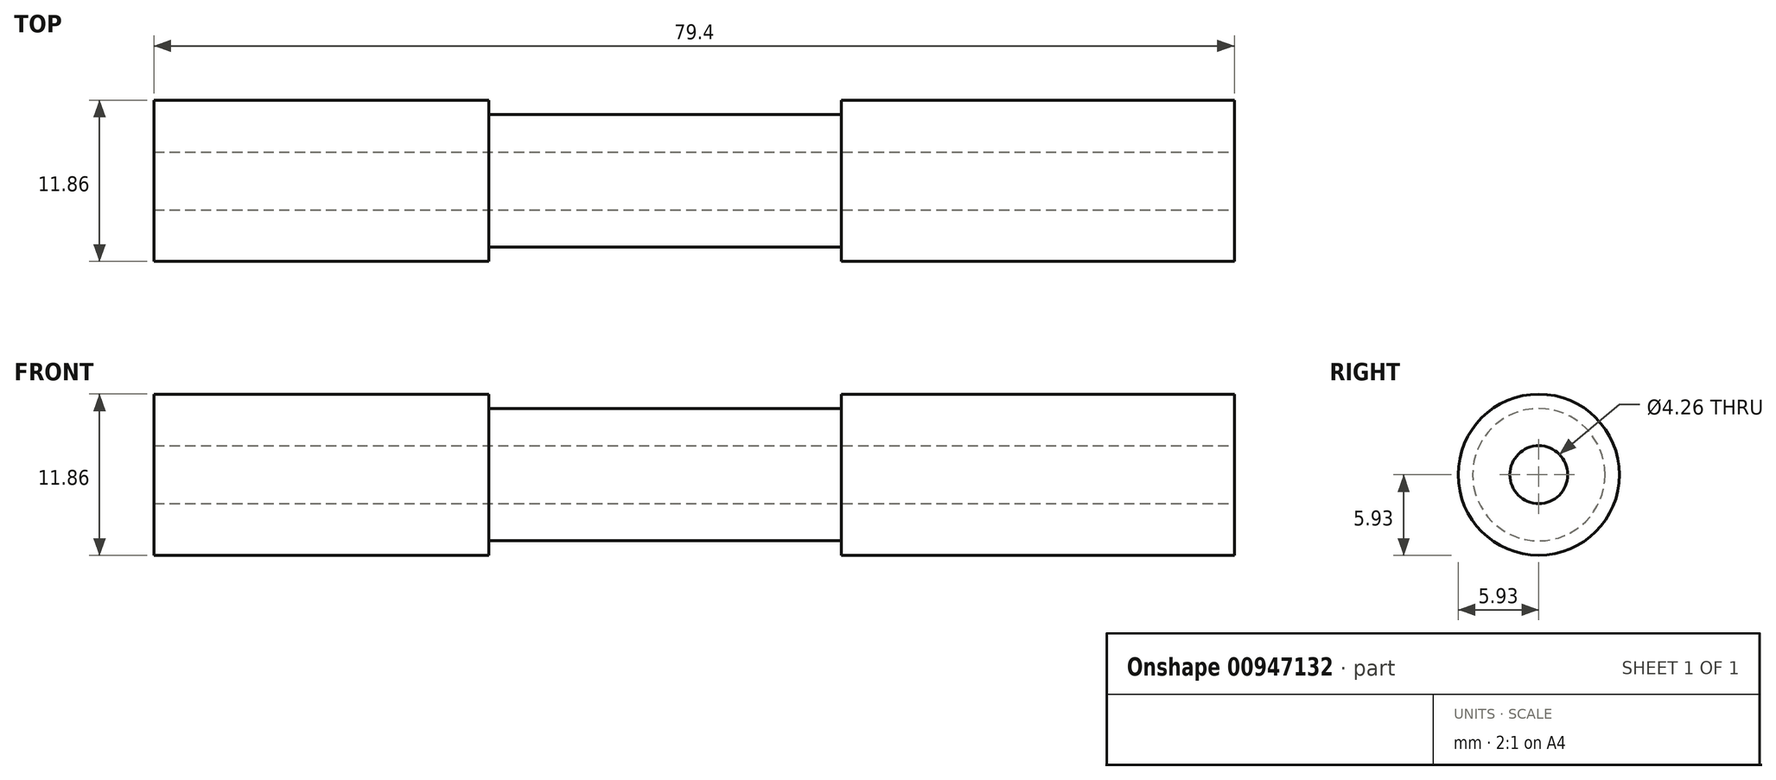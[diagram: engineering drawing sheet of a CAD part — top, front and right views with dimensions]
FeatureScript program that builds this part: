
annotation { "Feature Type Name" : "Feature", "Feature Type Description" : "" }
export const myFeature = defineFeature(function(context is Context, id is Id, definition is map)
    precondition{}
    {
        {
            var Q0;
            Q0=qCreatedBy(makeId("Right.planeOp"),FACE);
            var sketch = newSketch(context, id + "F0", { "sketchPlane" : qUnion([Q0])});
            skCircle(sketch, "E0", {"center": v(0, 0) * mm, "radius": 5.92 * mm});
            skSolve(sketch);
        }
        {
            var Q0;
            Q0=makeQuery(id+"F0.imprint","IMPRINT",FACE,{"disambiguationData":[TD([[makeQuery(id+"F0.imprint","IMPRINT",EDGE,{"derivedFrom":sQuery(id+"F0.wireOp",EDGE,"E0")}),1.0]])]});
            var Q1;
            Q1=sQuery(id+"F0.wireOp",EDGE,"E0");
            extrude(context, id + "F1", {"entities" : qUnion([Q0]), "surfaceEntities" : qUnion([Q1]), "depth" : 24.6 * mm, "offsetDistance" : 25 * mm});
        }
        {
            var Q0;
            Q0=makeQuery(id+"F1.opExtrude","CAP_FACE",FACE,{"disambiguationData":[OSD([sQuery(id+"F0.wireOp",EDGE,"E0")])],"isStart":false});
            var sketch = newSketch(context, id + "F2", { "sketchPlane" : qUnion([Q0])});
            skCircle(sketch, "E1", {"center": v(0, 0) * mm, "radius": 4.87 * mm});
            skSolve(sketch);
        }
        {
            var Q0;
            Q0=makeQuery(id+"F2.imprint","IMPRINT",FACE,{"disambiguationData":[TD([[makeQuery(id+"F2.imprint","IMPRINT",EDGE,{"derivedFrom":sQuery(id+"F2.wireOp",EDGE,"E1")}),1.0]])]});
            var Q1;
            Q1=sQuery(id+"F2.wireOp",EDGE,"E1");
            extrude(context, id + "F3", {"entities" : qUnion([Q0]), "operationType" : NewBodyOperationType.ADD, "surfaceEntities" : qUnion([Q1]), "depth" : 25.9 * mm, "offsetDistance" : 25 * mm});
        }
        {
            var Q0;
            Q0=makeQuery(id+"F3.opExtrude","CAP_FACE",FACE,{"disambiguationData":[OSD([sQuery(id+"F2.wireOp",EDGE,"E1")])],"isStart":false});
            var sketch = newSketch(context, id + "F4", { "sketchPlane" : qUnion([Q0])});
            skCircle(sketch, "E2", {"center": v(0, 0) * mm, "radius": 5.92 * mm});
            skSolve(sketch);
        }
        {
            var Q0;
            Q0=makeQuery(id+"F4.imprint","IMPRINT",FACE,{"disambiguationData":[TD([[makeQuery(id+"F4.imprint","IMPRINT",EDGE,{"derivedFrom":sQuery(id+"F4.wireOp",EDGE,"E2")}),1.0]])]});
            var Q1;
            Q1=makeQuery(id+"F4.imprint","IMPRINT",FACE,{"disambiguationData":[TD([[makeQuery(id+"F4.imprint","IMPRINT",EDGE,{"derivedFrom":makeQuery(id+"F3.opExtrude","CAP_EDGE",EDGE,{"disambiguationData":[OSD([sQuery(id+"F2.wireOp",EDGE,"E1")])],"isStart":false})}),1.0]])]});
            extrude(context, id + "F5", {"entities" : qUnion([Q0, Q1]), "operationType" : NewBodyOperationType.ADD, "depth" : 28.9 * mm, "offsetDistance" : 25 * mm});
        }
        {
            var Q0;
            Q0=makeQuery(id+"F5.opExtrude","CAP_FACE",FACE,{"disambiguationData":[OSD([sQuery(id+"F4.wireOp",EDGE,"E2")])],"isStart":false});
            var sketch = newSketch(context, id + "F6", { "sketchPlane" : qUnion([Q0])});
            skCircle(sketch, "E3", {"center": v(0, 0) * mm, "radius": 2.13 * mm});
            skSolve(sketch);
        }
        {
            var Q0;
            Q0=sQuery(id+"F6.wireOp",VERTEX,"E3.center");
            var Q1;
            Q1=makeQuery(id+"F1.opExtrude","SWEPT_BODY",BODY,{"disambiguationData":[OSD([sQuery(id+"F0.wireOp",EDGE,"E0")])]});
            hole(context, id + "F7", {"style" : HoleStyle.SIMPLE, "endStyle" : HoleEndStyle.THROUGH, "holeDiameter" : 4.26 * mm, "majorDiameter" : 3 * mm, "tappedDepth" : 5.25 * mm, "tapClearance" : 3, "startFromSketch" : true, "locations" : qUnion([Q0]), "scope" : qUnion([Q1])});
        }
    });
